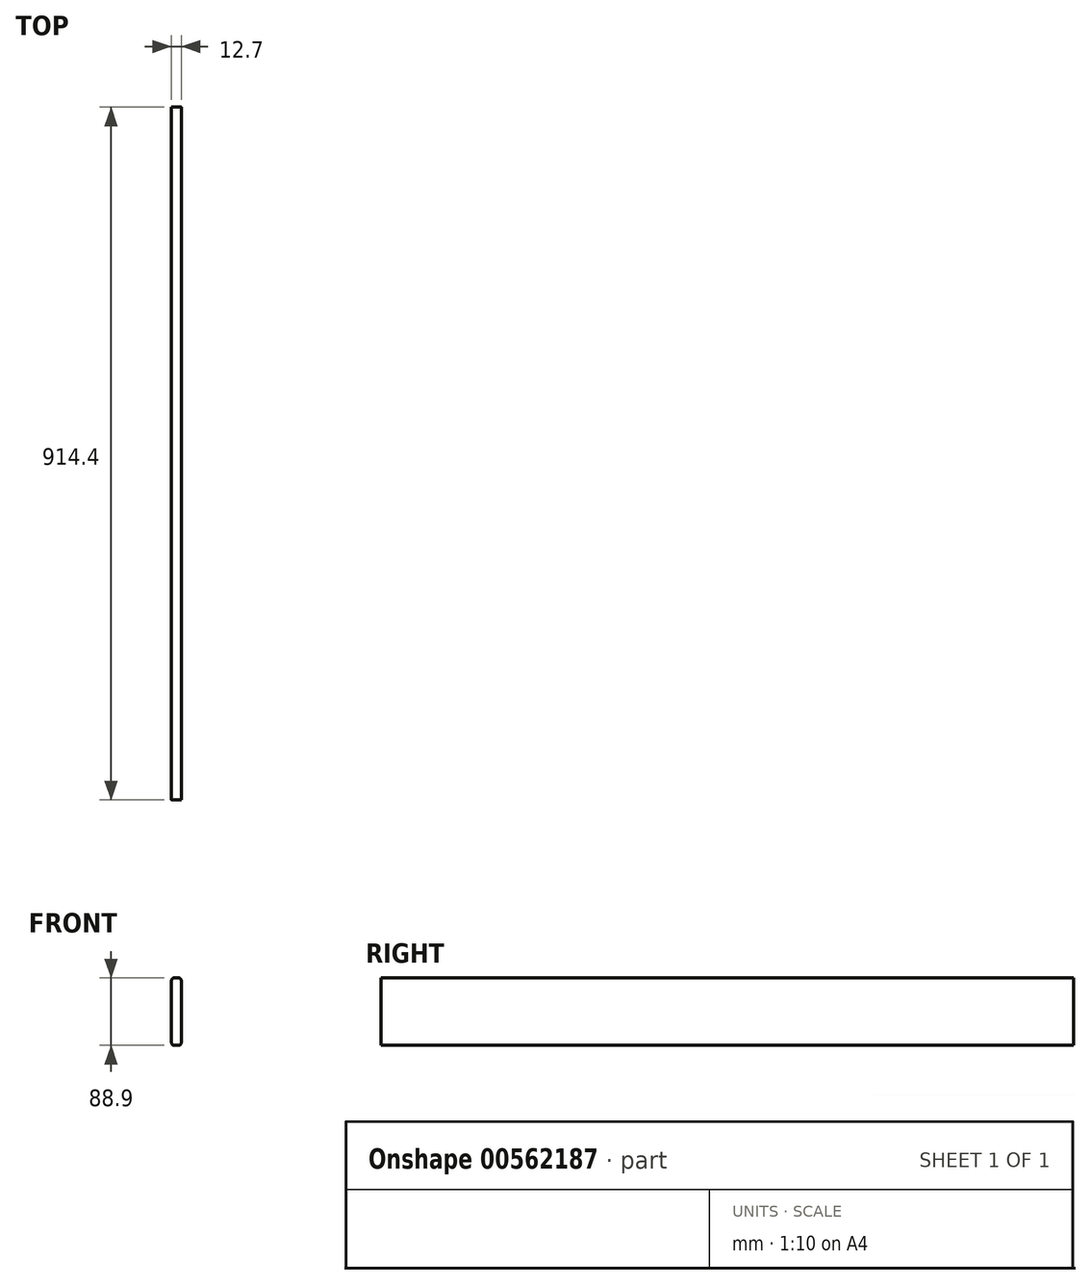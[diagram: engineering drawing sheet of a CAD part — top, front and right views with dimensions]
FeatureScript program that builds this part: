
annotation { "Feature Type Name" : "Feature", "Feature Type Description" : "" }
export const myFeature = defineFeature(function(context is Context, id is Id, definition is map)
    precondition{}
    {
        {
            var Q0;
            Q0=qCreatedBy(makeId("Front.planeOp"),FACE);
            var sketch = newSketch(context, id + "F0", { "sketchPlane" : qUnion([Q0])});
            skLineSegment(sketch, "E0.bottom", {"start": v(-3.17, 44.45) * mm, "end": v(3.17, 44.45) * mm});
            skLineSegment(sketch, "E0.top", {"start": v(-3.17, -44.45) * mm, "end": v(3.17, -44.45) * mm});
            skLineSegment(sketch, "E0.left", {"start": v(-6.35, 41.28) * mm, "end": v(-6.35, -41.28) * mm});
            skLineSegment(sketch, "E0.right", {"start": v(6.35, 41.28) * mm, "end": v(6.35, -41.28) * mm});
            skPoint(sketch, "E1.visualSharp", {"position": v(-6.35, 44.45) * mm});
            skArc(sketch, "E1.filletArc", {"start": v(-3.17, 44.45) * mm, "mid": v(-5.42, 43.52) * mm, "end": v(-6.35, 41.28) * mm});
            skPoint(sketch, "E2.visualSharp", {"position": v(6.35, 44.45) * mm});
            skArc(sketch, "E2.filletArc", {"start": v(6.35, 41.28) * mm, "mid": v(5.42, 43.52) * mm, "end": v(3.17, 44.45) * mm});
            skPoint(sketch, "E3.visualSharp", {"position": v(-6.35, -44.45) * mm});
            skArc(sketch, "E3.filletArc", {"start": v(-6.35, -41.28) * mm, "mid": v(-5.42, -43.52) * mm, "end": v(-3.17, -44.45) * mm});
            skPoint(sketch, "E4.visualSharp", {"position": v(6.35, -44.45) * mm});
            skArc(sketch, "E4.filletArc", {"start": v(3.17, -44.45) * mm, "mid": v(5.42, -43.52) * mm, "end": v(6.35, -41.28) * mm});
            skLineSegment(sketch, "E5", {"start": v(0, 0) * mm, "end": v(0, -44.45) * mm, "construction": true});
            skLineSegment(sketch, "E6", {"start": v(0, 0) * mm, "end": v(-6.35, 0) * mm, "construction": true});
            skSolve(sketch);
        }
        {
            var Q0;
            Q0=makeQuery(id+"F0.imprint","IMPRINT",FACE,{"disambiguationData":[TD([[makeQuery(id+"F0.imprint","IMPRINT",EDGE,{"derivedFrom":sQuery(id+"F0.wireOp",EDGE,"E0.bottom")}),-1.0]])]});
            extrude(context, id + "F1", {"entities" : qUnion([Q0]), "depth" : 914.4 * mm, "offsetDistance" : 25.4 * mm});
        }
    });
